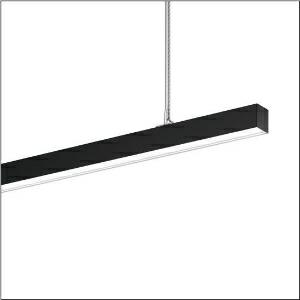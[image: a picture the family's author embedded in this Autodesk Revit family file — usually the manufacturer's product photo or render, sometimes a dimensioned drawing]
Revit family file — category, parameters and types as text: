
# Revit family: silica_r__21_51mx30dc39bb_25b6
name_source: partatom
category: Lighting Fixtures
units: mm (PartAtom-declared; Revit-internal decimal feet)

## family parameters
Cut with Voids When Loaded = No
Host = Face
Light Source = No
Part Type = Normal
Room Calculation Point = No
Round Connector Dimension = Use Diameter
Shared = No

## types (1)
- --- (1 x LED, 10520 lm, 68.3 W, 3000K)
    Apparent Load = 68 VA
    CIE Flux Codes = 47 79 96 57 100
    Color Rendering = 80
    Color Temperature = 3000K
    Default Elevation = 1800 mm
    Description = Silica® 21, office luminaire, primary optical cover: cover, of PMMA, opal, light emission: direct/indirect distribution, primary light characteristic: symmetric, installation type: suspended mounting, LED, rated luminous flux: 10.520lm, luminous efficacy: 154lm/W, light colour: 830, colour temperature: 3000K, control gear: DALI 2, with terminal, 3+2-pole, max. 2.5mm², mains connection: 220..240V, AC, 50/60Hz, rated input power: 68.3W, luminaire housing, of aluminium, matt jet black (RAL 9005), length: 3.004mm, width: 53mm, height: 53mm, protection rating (complete): IP20, insulation class (complete): insulation class I (protective earthing), certification: CE, permissible operating ambient temperature: 0..+35°C, standard: EN 50419, packaging unit: 1 piece
    Height = 53 mm
    Lamp = 1 x LED
    Lamp Light Flux = 10520 lm
    Lamp Power = 68.3 W
    Lamp count = 1
    Length = 3004 mm
    Luminous efficacy = 154 lm/W
    Manufacturer = Siteco
    ModVariant = No
    Model = 51MX30DC39BB
    Mounting Place = Ceiling
    Mounting Type = Pendant
    Number of Poles = 1
    OnlyDefault = Yes
    Power Factor = 1
    Product Name = Silica® 21
    Product group = office luminaire | ceiling pendant
    ProductGroupID = 903
    Protection Class = Protection class I
    Protection Degree = IP 20
    RLX_Detail_Level = 1
    RLX_Emergency_Light_Flux = 0 lm
    RLX_Emergency_Type = 0
    RLX_Emergency_Type_DB = No
    RlxData = <blob elided: 26081 chars, md5=c9c565d2>
    Socket = socket
    Standby Power = 0 W
    System Light Flux = 10520 lm
    System Power = 68 W
    Type Comments = factory setting: luminous flux: 100 % | dim-lin: 254 | 233 mA
    Type Image = l_1335856.jpg
    URL = http://relux.com
    VarID = @adj_138747
    Voltage = 0 V
    Weight = 0.00 kg
    Width = 53 mm

## geometry (parser evidence)
native form markers: Blend x4, Sweep x13
no freeform markers — native parametric forms only
